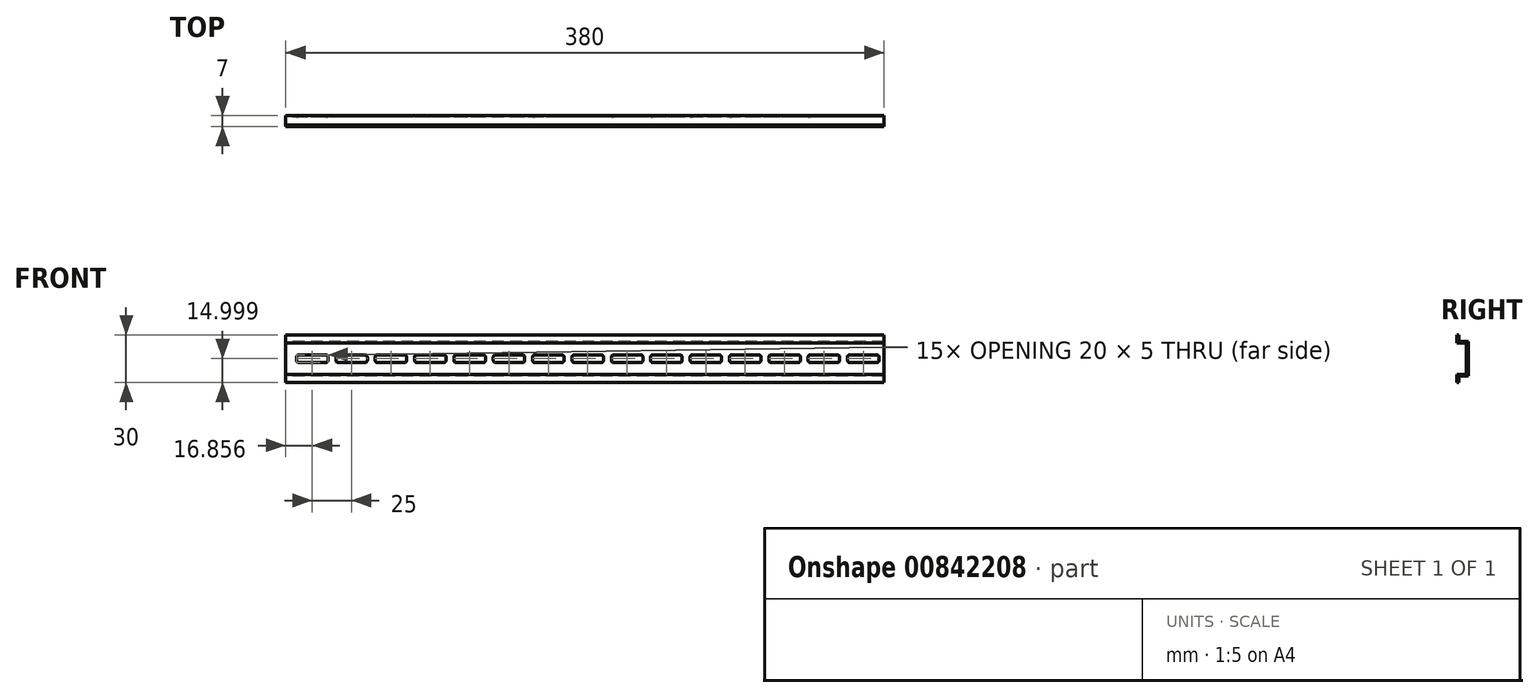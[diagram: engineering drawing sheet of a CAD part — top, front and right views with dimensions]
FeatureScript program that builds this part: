
annotation { "Feature Type Name" : "Feature", "Feature Type Description" : "" }
export const myFeature = defineFeature(function(context is Context, id is Id, definition is map)
    precondition{}
    {
        {
            var Q0;
            Q0=qCreatedBy(makeId("Right.planeOp"),FACE);
            var sketch = newSketch(context, id + "F0", { "sketchPlane" : qUnion([Q0])});
            skLineSegment(sketch, "E0", {"start": v(0, -3.03) * mm, "end": v(0, -25.03) * mm});
            skLineSegment(sketch, "E1", {"start": v(0, -25.03) * mm, "end": v(-6, -25.03) * mm});
            skLineSegment(sketch, "E2", {"start": v(-6, -25.03) * mm, "end": v(-6, -29.03) * mm});
            skLineSegment(sketch, "E3", {"start": v(0, -3.03) * mm, "end": v(-6, -3.03) * mm});
            skLineSegment(sketch, "E4", {"start": v(-6, -3.03) * mm, "end": v(-6, 0.97) * mm});
            skLineSegment(sketch, "E5.1", {"start": v(-7, -24.03) * mm, "end": v(-7, -29.03) * mm});
            skLineSegment(sketch, "E5.2", {"start": v(-1, -24.03) * mm, "end": v(-7, -24.03) * mm});
            skLineSegment(sketch, "E5.3", {"start": v(-1, -4.03) * mm, "end": v(-1, -24.03) * mm});
            skLineSegment(sketch, "E5.4", {"start": v(-1, -4.03) * mm, "end": v(-7, -4.03) * mm});
            skLineSegment(sketch, "E6", {"start": v(-6, -29.03) * mm, "end": v(-7, -29.03) * mm});
            skLineSegment(sketch, "E7", {"start": v(-6, 0.97) * mm, "end": v(-7, 0.97) * mm});
            skLineSegment(sketch, "E8", {"start": v(-7, -4.03) * mm, "end": v(-7, 0.97) * mm});
            skSolve(sketch);
        }
        {
            var Q0;
            Q0=makeQuery(id+"F0.imprint","IMPRINT",FACE,{"disambiguationData":[TD([[makeQuery(id+"F0.imprint","IMPRINT",EDGE,{"derivedFrom":sQuery(id+"F0.wireOp",EDGE,"E0")}),-1.0]])]});
            extrude(context, id + "F1", {"entities" : qUnion([Q0]), "depth" : 380 * mm, "offsetDistance" : 25 * mm});
        }
        {
            var Q0;
            Q0=makeQuery(id+"F1.opExtrude","SWEPT_FACE",FACE,{"disambiguationData":[OSD([sQuery(id+"F0.wireOp",EDGE,"E5.3")])]});
            var sketch = newSketch(context, id + "F2", { "sketchPlane" : qUnion([Q0])});
            skLineSegment(sketch, "E9", {"start": v(0, -14.03) * mm, "end": v(380, -14.03) * mm});
            skLineSegment(sketch, "E10.bottom", {"start": v(25.36, -16.53) * mm, "end": v(8.36, -16.53) * mm});
            skLineSegment(sketch, "E10.top", {"start": v(25.36, -11.53) * mm, "end": v(8.36, -11.53) * mm});
            skLineSegment(sketch, "E10.left", {"start": v(26.86, -15.03) * mm, "end": v(26.86, -13.03) * mm});
            skLineSegment(sketch, "E10.right", {"start": v(6.86, -15.03) * mm, "end": v(6.86, -13.03) * mm});
            skPoint(sketch, "E10.middle", {"position": v(16.86, -14.03) * mm});
            skPoint(sketch, "E11.visualSharp", {"position": v(26.86, -11.53) * mm});
            skArc(sketch, "E11.filletArc", {"start": v(26.86, -13.03) * mm, "mid": v(26.42, -11.97) * mm, "end": v(25.36, -11.53) * mm});
            skPoint(sketch, "E12.visualSharp", {"position": v(26.86, -16.53) * mm});
            skArc(sketch, "E12.filletArc", {"start": v(25.36, -16.53) * mm, "mid": v(26.42, -16.1) * mm, "end": v(26.86, -15.03) * mm});
            skPoint(sketch, "E13.visualSharp", {"position": v(6.86, -11.53) * mm});
            skArc(sketch, "E13.filletArc", {"start": v(8.36, -11.53) * mm, "mid": v(7.3, -11.97) * mm, "end": v(6.86, -13.03) * mm});
            skPoint(sketch, "E14.visualSharp", {"position": v(6.86, -16.53) * mm});
            skArc(sketch, "E14.filletArc", {"start": v(6.86, -15.03) * mm, "mid": v(7.3, -16.1) * mm, "end": v(8.36, -16.53) * mm});
            skLineSegment(sketch, "E15.1.0.0", {"start": v(50.36, -11.53) * mm, "end": v(33.36, -11.53) * mm});
            skLineSegment(sketch, "E15.1.0.1", {"start": v(50.36, -16.53) * mm, "end": v(33.36, -16.53) * mm});
            skArc(sketch, "E15.1.0.2", {"start": v(51.86, -13.03) * mm, "mid": v(51.42, -11.97) * mm, "end": v(50.36, -11.53) * mm});
            skArc(sketch, "E15.1.0.3", {"start": v(50.36, -16.53) * mm, "mid": v(51.42, -16.1) * mm, "end": v(51.86, -15.03) * mm});
            skArc(sketch, "E15.1.0.4", {"start": v(33.36, -11.53) * mm, "mid": v(32.3, -11.97) * mm, "end": v(31.86, -13.03) * mm});
            skArc(sketch, "E15.1.0.5", {"start": v(31.86, -15.03) * mm, "mid": v(32.3, -16.1) * mm, "end": v(33.36, -16.53) * mm});
            skLineSegment(sketch, "E15.2.0.0", {"start": v(75.36, -11.53) * mm, "end": v(58.36, -11.53) * mm});
            skLineSegment(sketch, "E15.2.0.1", {"start": v(75.36, -16.53) * mm, "end": v(58.36, -16.53) * mm});
            skArc(sketch, "E15.2.0.2", {"start": v(76.86, -13.03) * mm, "mid": v(76.42, -11.97) * mm, "end": v(75.36, -11.53) * mm});
            skArc(sketch, "E15.2.0.3", {"start": v(75.36, -16.53) * mm, "mid": v(76.42, -16.1) * mm, "end": v(76.86, -15.03) * mm});
            skArc(sketch, "E15.2.0.4", {"start": v(58.36, -11.53) * mm, "mid": v(57.3, -11.97) * mm, "end": v(56.86, -13.03) * mm});
            skArc(sketch, "E15.2.0.5", {"start": v(56.86, -15.03) * mm, "mid": v(57.3, -16.1) * mm, "end": v(58.36, -16.53) * mm});
            skLineSegment(sketch, "E15.3.0.0", {"start": v(100.36, -11.53) * mm, "end": v(83.36, -11.53) * mm});
            skLineSegment(sketch, "E15.3.0.1", {"start": v(100.36, -16.53) * mm, "end": v(83.36, -16.53) * mm});
            skArc(sketch, "E15.3.0.2", {"start": v(101.86, -13.03) * mm, "mid": v(101.42, -11.97) * mm, "end": v(100.36, -11.53) * mm});
            skArc(sketch, "E15.3.0.3", {"start": v(100.36, -16.53) * mm, "mid": v(101.42, -16.1) * mm, "end": v(101.86, -15.03) * mm});
            skArc(sketch, "E15.3.0.4", {"start": v(83.36, -11.53) * mm, "mid": v(82.3, -11.97) * mm, "end": v(81.86, -13.03) * mm});
            skArc(sketch, "E15.3.0.5", {"start": v(81.86, -15.03) * mm, "mid": v(82.3, -16.1) * mm, "end": v(83.36, -16.53) * mm});
            skLineSegment(sketch, "E15.4.0.0", {"start": v(125.36, -11.53) * mm, "end": v(108.36, -11.53) * mm});
            skLineSegment(sketch, "E15.4.0.1", {"start": v(125.36, -16.53) * mm, "end": v(108.36, -16.53) * mm});
            skArc(sketch, "E15.4.0.2", {"start": v(126.86, -13.03) * mm, "mid": v(126.42, -11.97) * mm, "end": v(125.36, -11.53) * mm});
            skArc(sketch, "E15.4.0.3", {"start": v(125.36, -16.53) * mm, "mid": v(126.42, -16.1) * mm, "end": v(126.86, -15.03) * mm});
            skArc(sketch, "E15.4.0.4", {"start": v(108.36, -11.53) * mm, "mid": v(107.3, -11.97) * mm, "end": v(106.86, -13.03) * mm});
            skArc(sketch, "E15.4.0.5", {"start": v(106.86, -15.03) * mm, "mid": v(107.3, -16.1) * mm, "end": v(108.36, -16.53) * mm});
            skLineSegment(sketch, "E15.5.0.0", {"start": v(150.36, -11.53) * mm, "end": v(133.36, -11.53) * mm});
            skLineSegment(sketch, "E15.5.0.1", {"start": v(150.36, -16.53) * mm, "end": v(133.36, -16.53) * mm});
            skArc(sketch, "E15.5.0.2", {"start": v(151.86, -13.03) * mm, "mid": v(151.42, -11.97) * mm, "end": v(150.36, -11.53) * mm});
            skArc(sketch, "E15.5.0.3", {"start": v(150.36, -16.53) * mm, "mid": v(151.42, -16.1) * mm, "end": v(151.86, -15.03) * mm});
            skArc(sketch, "E15.5.0.4", {"start": v(133.36, -11.53) * mm, "mid": v(132.3, -11.97) * mm, "end": v(131.86, -13.03) * mm});
            skArc(sketch, "E15.5.0.5", {"start": v(131.86, -15.03) * mm, "mid": v(132.3, -16.1) * mm, "end": v(133.36, -16.53) * mm});
            skLineSegment(sketch, "E15.6.0.0", {"start": v(175.36, -11.53) * mm, "end": v(158.36, -11.53) * mm});
            skLineSegment(sketch, "E15.6.0.1", {"start": v(175.36, -16.53) * mm, "end": v(158.36, -16.53) * mm});
            skArc(sketch, "E15.6.0.2", {"start": v(176.86, -13.03) * mm, "mid": v(176.42, -11.97) * mm, "end": v(175.36, -11.53) * mm});
            skArc(sketch, "E15.6.0.3", {"start": v(175.36, -16.53) * mm, "mid": v(176.42, -16.1) * mm, "end": v(176.86, -15.03) * mm});
            skArc(sketch, "E15.6.0.4", {"start": v(158.36, -11.53) * mm, "mid": v(157.3, -11.97) * mm, "end": v(156.86, -13.03) * mm});
            skArc(sketch, "E15.6.0.5", {"start": v(156.86, -15.03) * mm, "mid": v(157.3, -16.1) * mm, "end": v(158.36, -16.53) * mm});
            skLineSegment(sketch, "E15.7.0.0", {"start": v(200.36, -11.53) * mm, "end": v(183.36, -11.53) * mm});
            skLineSegment(sketch, "E15.7.0.1", {"start": v(200.36, -16.53) * mm, "end": v(183.36, -16.53) * mm});
            skArc(sketch, "E15.7.0.2", {"start": v(201.86, -13.03) * mm, "mid": v(201.42, -11.97) * mm, "end": v(200.36, -11.53) * mm});
            skArc(sketch, "E15.7.0.3", {"start": v(200.36, -16.53) * mm, "mid": v(201.42, -16.1) * mm, "end": v(201.86, -15.03) * mm});
            skArc(sketch, "E15.7.0.4", {"start": v(183.36, -11.53) * mm, "mid": v(182.3, -11.97) * mm, "end": v(181.86, -13.03) * mm});
            skArc(sketch, "E15.7.0.5", {"start": v(181.86, -15.03) * mm, "mid": v(182.3, -16.1) * mm, "end": v(183.36, -16.53) * mm});
            skLineSegment(sketch, "E15.8.0.0", {"start": v(225.36, -11.53) * mm, "end": v(208.36, -11.53) * mm});
            skLineSegment(sketch, "E15.8.0.1", {"start": v(225.36, -16.53) * mm, "end": v(208.36, -16.53) * mm});
            skArc(sketch, "E15.8.0.2", {"start": v(226.86, -13.03) * mm, "mid": v(226.42, -11.97) * mm, "end": v(225.36, -11.53) * mm});
            skArc(sketch, "E15.8.0.3", {"start": v(225.36, -16.53) * mm, "mid": v(226.42, -16.1) * mm, "end": v(226.86, -15.03) * mm});
            skArc(sketch, "E15.8.0.4", {"start": v(208.36, -11.53) * mm, "mid": v(207.3, -11.97) * mm, "end": v(206.86, -13.03) * mm});
            skArc(sketch, "E15.8.0.5", {"start": v(206.86, -15.03) * mm, "mid": v(207.3, -16.1) * mm, "end": v(208.36, -16.53) * mm});
            skLineSegment(sketch, "E15.9.0.0", {"start": v(250.36, -11.53) * mm, "end": v(233.36, -11.53) * mm});
            skLineSegment(sketch, "E15.9.0.1", {"start": v(250.36, -16.53) * mm, "end": v(233.36, -16.53) * mm});
            skArc(sketch, "E15.9.0.2", {"start": v(251.86, -13.03) * mm, "mid": v(251.42, -11.97) * mm, "end": v(250.36, -11.53) * mm});
            skArc(sketch, "E15.9.0.3", {"start": v(250.36, -16.53) * mm, "mid": v(251.42, -16.1) * mm, "end": v(251.86, -15.03) * mm});
            skArc(sketch, "E15.9.0.4", {"start": v(233.36, -11.53) * mm, "mid": v(232.3, -11.97) * mm, "end": v(231.86, -13.03) * mm});
            skArc(sketch, "E15.9.0.5", {"start": v(231.86, -15.03) * mm, "mid": v(232.3, -16.1) * mm, "end": v(233.36, -16.53) * mm});
            skLineSegment(sketch, "E15.10.0.0", {"start": v(275.36, -11.53) * mm, "end": v(258.36, -11.53) * mm});
            skLineSegment(sketch, "E15.10.0.1", {"start": v(275.36, -16.53) * mm, "end": v(258.36, -16.53) * mm});
            skArc(sketch, "E15.10.0.2", {"start": v(276.86, -13.03) * mm, "mid": v(276.42, -11.97) * mm, "end": v(275.36, -11.53) * mm});
            skArc(sketch, "E15.10.0.3", {"start": v(275.36, -16.53) * mm, "mid": v(276.42, -16.1) * mm, "end": v(276.86, -15.03) * mm});
            skArc(sketch, "E15.10.0.4", {"start": v(258.36, -11.53) * mm, "mid": v(257.3, -11.97) * mm, "end": v(256.86, -13.03) * mm});
            skArc(sketch, "E15.10.0.5", {"start": v(256.86, -15.03) * mm, "mid": v(257.3, -16.1) * mm, "end": v(258.36, -16.53) * mm});
            skLineSegment(sketch, "E15.11.0.0", {"start": v(300.36, -11.53) * mm, "end": v(283.36, -11.53) * mm});
            skLineSegment(sketch, "E15.11.0.1", {"start": v(300.36, -16.53) * mm, "end": v(283.36, -16.53) * mm});
            skArc(sketch, "E15.11.0.2", {"start": v(301.86, -13.03) * mm, "mid": v(301.42, -11.97) * mm, "end": v(300.36, -11.53) * mm});
            skArc(sketch, "E15.11.0.3", {"start": v(300.36, -16.53) * mm, "mid": v(301.42, -16.1) * mm, "end": v(301.86, -15.03) * mm});
            skArc(sketch, "E15.11.0.4", {"start": v(283.36, -11.53) * mm, "mid": v(282.3, -11.97) * mm, "end": v(281.86, -13.03) * mm});
            skArc(sketch, "E15.11.0.5", {"start": v(281.86, -15.03) * mm, "mid": v(282.3, -16.1) * mm, "end": v(283.36, -16.53) * mm});
            skLineSegment(sketch, "E15.12.0.0", {"start": v(325.36, -11.53) * mm, "end": v(308.36, -11.53) * mm});
            skLineSegment(sketch, "E15.12.0.1", {"start": v(325.36, -16.53) * mm, "end": v(308.36, -16.53) * mm});
            skArc(sketch, "E15.12.0.2", {"start": v(326.86, -13.03) * mm, "mid": v(326.42, -11.97) * mm, "end": v(325.36, -11.53) * mm});
            skArc(sketch, "E15.12.0.3", {"start": v(325.36, -16.53) * mm, "mid": v(326.42, -16.1) * mm, "end": v(326.86, -15.03) * mm});
            skArc(sketch, "E15.12.0.4", {"start": v(308.36, -11.53) * mm, "mid": v(307.3, -11.97) * mm, "end": v(306.86, -13.03) * mm});
            skArc(sketch, "E15.12.0.5", {"start": v(306.86, -15.03) * mm, "mid": v(307.3, -16.1) * mm, "end": v(308.36, -16.53) * mm});
            skLineSegment(sketch, "E15.13.0.0", {"start": v(350.36, -11.53) * mm, "end": v(333.36, -11.53) * mm});
            skLineSegment(sketch, "E15.13.0.1", {"start": v(350.36, -16.53) * mm, "end": v(333.36, -16.53) * mm});
            skArc(sketch, "E15.13.0.2", {"start": v(351.86, -13.03) * mm, "mid": v(351.42, -11.97) * mm, "end": v(350.36, -11.53) * mm});
            skArc(sketch, "E15.13.0.3", {"start": v(350.36, -16.53) * mm, "mid": v(351.42, -16.1) * mm, "end": v(351.86, -15.03) * mm});
            skArc(sketch, "E15.13.0.4", {"start": v(333.36, -11.53) * mm, "mid": v(332.3, -11.97) * mm, "end": v(331.86, -13.03) * mm});
            skArc(sketch, "E15.13.0.5", {"start": v(331.86, -15.03) * mm, "mid": v(332.3, -16.1) * mm, "end": v(333.36, -16.53) * mm});
            skLineSegment(sketch, "E15.14.0.0", {"start": v(375.36, -11.53) * mm, "end": v(358.36, -11.53) * mm});
            skLineSegment(sketch, "E15.14.0.1", {"start": v(375.36, -16.53) * mm, "end": v(358.36, -16.53) * mm});
            skArc(sketch, "E15.14.0.2", {"start": v(376.86, -13.03) * mm, "mid": v(376.42, -11.97) * mm, "end": v(375.36, -11.53) * mm});
            skArc(sketch, "E15.14.0.3", {"start": v(375.36, -16.53) * mm, "mid": v(376.42, -16.1) * mm, "end": v(376.86, -15.03) * mm});
            skArc(sketch, "E15.14.0.4", {"start": v(358.36, -11.53) * mm, "mid": v(357.3, -11.97) * mm, "end": v(356.86, -13.03) * mm});
            skArc(sketch, "E15.14.0.5", {"start": v(356.86, -15.03) * mm, "mid": v(357.3, -16.1) * mm, "end": v(358.36, -16.53) * mm});
            skLineSegment(sketch, "E15.direction1", {"start": v(8.36, -11.53) * mm, "end": v(33.36, -11.53) * mm, "construction": true});
            skLineSegment(sketch, "E16.1.0.0", {"start": v(31.86, -15.03) * mm, "end": v(31.86, -13.03) * mm});
            skLineSegment(sketch, "E16.1.0.1", {"start": v(51.86, -15.03) * mm, "end": v(51.86, -13.03) * mm});
            skLineSegment(sketch, "E16.2.0.0", {"start": v(56.86, -15.03) * mm, "end": v(56.86, -13.03) * mm});
            skLineSegment(sketch, "E16.2.0.1", {"start": v(76.86, -15.03) * mm, "end": v(76.86, -13.03) * mm});
            skLineSegment(sketch, "E16.3.0.0", {"start": v(81.86, -15.03) * mm, "end": v(81.86, -13.03) * mm});
            skLineSegment(sketch, "E16.3.0.1", {"start": v(101.86, -15.03) * mm, "end": v(101.86, -13.03) * mm});
            skLineSegment(sketch, "E16.4.0.0", {"start": v(106.86, -15.03) * mm, "end": v(106.86, -13.03) * mm});
            skLineSegment(sketch, "E16.4.0.1", {"start": v(126.86, -15.03) * mm, "end": v(126.86, -13.03) * mm});
            skLineSegment(sketch, "E16.5.0.0", {"start": v(131.86, -15.03) * mm, "end": v(131.86, -13.03) * mm});
            skLineSegment(sketch, "E16.5.0.1", {"start": v(151.86, -15.03) * mm, "end": v(151.86, -13.03) * mm});
            skLineSegment(sketch, "E16.6.0.0", {"start": v(156.86, -15.03) * mm, "end": v(156.86, -13.03) * mm});
            skLineSegment(sketch, "E16.6.0.1", {"start": v(176.86, -15.03) * mm, "end": v(176.86, -13.03) * mm});
            skLineSegment(sketch, "E16.7.0.0", {"start": v(181.86, -15.03) * mm, "end": v(181.86, -13.03) * mm});
            skLineSegment(sketch, "E16.7.0.1", {"start": v(201.86, -15.03) * mm, "end": v(201.86, -13.03) * mm});
            skLineSegment(sketch, "E16.8.0.0", {"start": v(206.86, -15.03) * mm, "end": v(206.86, -13.03) * mm});
            skLineSegment(sketch, "E16.8.0.1", {"start": v(226.86, -15.03) * mm, "end": v(226.86, -13.03) * mm});
            skLineSegment(sketch, "E16.9.0.0", {"start": v(231.86, -15.03) * mm, "end": v(231.86, -13.03) * mm});
            skLineSegment(sketch, "E16.9.0.1", {"start": v(251.86, -15.03) * mm, "end": v(251.86, -13.03) * mm});
            skLineSegment(sketch, "E16.10.0.0", {"start": v(256.86, -15.03) * mm, "end": v(256.86, -13.03) * mm});
            skLineSegment(sketch, "E16.10.0.1", {"start": v(276.86, -15.03) * mm, "end": v(276.86, -13.03) * mm});
            skLineSegment(sketch, "E16.11.0.0", {"start": v(281.86, -15.03) * mm, "end": v(281.86, -13.03) * mm});
            skLineSegment(sketch, "E16.11.0.1", {"start": v(301.86, -15.03) * mm, "end": v(301.86, -13.03) * mm});
            skLineSegment(sketch, "E16.12.0.0", {"start": v(306.86, -15.03) * mm, "end": v(306.86, -13.03) * mm});
            skLineSegment(sketch, "E16.12.0.1", {"start": v(326.86, -15.03) * mm, "end": v(326.86, -13.03) * mm});
            skLineSegment(sketch, "E16.13.0.0", {"start": v(331.86, -15.03) * mm, "end": v(331.86, -13.03) * mm});
            skLineSegment(sketch, "E16.13.0.1", {"start": v(351.86, -15.03) * mm, "end": v(351.86, -13.03) * mm});
            skLineSegment(sketch, "E16.14.0.0", {"start": v(356.86, -15.03) * mm, "end": v(356.86, -13.03) * mm});
            skLineSegment(sketch, "E16.14.0.1", {"start": v(376.86, -15.03) * mm, "end": v(376.86, -13.03) * mm});
            skLineSegment(sketch, "E16.direction1", {"start": v(6.86, -15.03) * mm, "end": v(31.86, -15.03) * mm, "construction": true});
            skSolve(sketch);
        }
        {
            var Q0;
            Q0=makeQuery(id+"F2.imprint","IMPRINT",FACE,{"disambiguationData":[TD([[makeQuery(id+"F2.imprint","IMPRINT",EDGE,{"derivedFrom":sQuery(id+"F2.wireOp",EDGE,"E10.top")}),1.0]])]});
            var Q1;
            Q1=makeQuery(id+"F2.imprint","IMPRINT",FACE,{"disambiguationData":[TD([[makeQuery(id+"F2.imprint","IMPRINT",EDGE,{"derivedFrom":sQuery(id+"F2.wireOp",EDGE,"E10.bottom")}),-1.0]])]});
            var Q2;
            Q2=makeQuery(id+"F2.imprint","IMPRINT",FACE,{"disambiguationData":[TD([[makeQuery(id+"F2.imprint","IMPRINT",EDGE,{"derivedFrom":sQuery(id+"F2.wireOp",EDGE,"E15.1.0.0")}),1.0]])]});
            var Q3;
            Q3=makeQuery(id+"F2.imprint","IMPRINT",FACE,{"disambiguationData":[TD([[makeQuery(id+"F2.imprint","IMPRINT",EDGE,{"derivedFrom":sQuery(id+"F2.wireOp",EDGE,"E15.1.0.1")}),-1.0]])]});
            var Q4;
            Q4=makeQuery(id+"F2.imprint","IMPRINT",FACE,{"disambiguationData":[TD([[makeQuery(id+"F2.imprint","IMPRINT",EDGE,{"derivedFrom":sQuery(id+"F2.wireOp",EDGE,"E15.2.0.0")}),1.0]])]});
            var Q5;
            Q5=makeQuery(id+"F2.imprint","IMPRINT",FACE,{"disambiguationData":[TD([[makeQuery(id+"F2.imprint","IMPRINT",EDGE,{"derivedFrom":sQuery(id+"F2.wireOp",EDGE,"E15.2.0.1")}),-1.0]])]});
            var Q6;
            Q6=makeQuery(id+"F2.imprint","IMPRINT",FACE,{"disambiguationData":[TD([[makeQuery(id+"F2.imprint","IMPRINT",EDGE,{"derivedFrom":sQuery(id+"F2.wireOp",EDGE,"E15.3.0.0")}),1.0]])]});
            var Q7;
            Q7=makeQuery(id+"F2.imprint","IMPRINT",FACE,{"disambiguationData":[TD([[makeQuery(id+"F2.imprint","IMPRINT",EDGE,{"derivedFrom":sQuery(id+"F2.wireOp",EDGE,"E15.3.0.1")}),-1.0]])]});
            var Q8;
            Q8=makeQuery(id+"F2.imprint","IMPRINT",FACE,{"disambiguationData":[TD([[makeQuery(id+"F2.imprint","IMPRINT",EDGE,{"derivedFrom":sQuery(id+"F2.wireOp",EDGE,"E15.4.0.0")}),1.0]])]});
            var Q9;
            Q9=makeQuery(id+"F2.imprint","IMPRINT",FACE,{"disambiguationData":[TD([[makeQuery(id+"F2.imprint","IMPRINT",EDGE,{"derivedFrom":sQuery(id+"F2.wireOp",EDGE,"E15.4.0.1")}),-1.0]])]});
            var Q10;
            Q10=makeQuery(id+"F2.imprint","IMPRINT",FACE,{"disambiguationData":[TD([[makeQuery(id+"F2.imprint","IMPRINT",EDGE,{"derivedFrom":sQuery(id+"F2.wireOp",EDGE,"E15.5.0.0")}),1.0]])]});
            var Q11;
            Q11=makeQuery(id+"F2.imprint","IMPRINT",FACE,{"disambiguationData":[TD([[makeQuery(id+"F2.imprint","IMPRINT",EDGE,{"derivedFrom":sQuery(id+"F2.wireOp",EDGE,"E15.5.0.1")}),-1.0]])]});
            var Q12;
            Q12=makeQuery(id+"F2.imprint","IMPRINT",FACE,{"disambiguationData":[TD([[makeQuery(id+"F2.imprint","IMPRINT",EDGE,{"derivedFrom":sQuery(id+"F2.wireOp",EDGE,"E15.6.0.1")}),-1.0]])]});
            var Q13;
            Q13=makeQuery(id+"F2.imprint","IMPRINT",FACE,{"disambiguationData":[TD([[makeQuery(id+"F2.imprint","IMPRINT",EDGE,{"derivedFrom":sQuery(id+"F2.wireOp",EDGE,"E15.6.0.0")}),1.0]])]});
            var Q14;
            Q14=makeQuery(id+"F2.imprint","IMPRINT",FACE,{"disambiguationData":[TD([[makeQuery(id+"F2.imprint","IMPRINT",EDGE,{"derivedFrom":sQuery(id+"F2.wireOp",EDGE,"E15.7.0.0")}),1.0]])]});
            var Q15;
            Q15=makeQuery(id+"F2.imprint","IMPRINT",FACE,{"disambiguationData":[TD([[makeQuery(id+"F2.imprint","IMPRINT",EDGE,{"derivedFrom":sQuery(id+"F2.wireOp",EDGE,"E15.7.0.1")}),-1.0]])]});
            var Q16;
            Q16=makeQuery(id+"F2.imprint","IMPRINT",FACE,{"disambiguationData":[TD([[makeQuery(id+"F2.imprint","IMPRINT",EDGE,{"derivedFrom":sQuery(id+"F2.wireOp",EDGE,"E15.8.0.1")}),-1.0]])]});
            var Q17;
            Q17=makeQuery(id+"F2.imprint","IMPRINT",FACE,{"disambiguationData":[TD([[makeQuery(id+"F2.imprint","IMPRINT",EDGE,{"derivedFrom":sQuery(id+"F2.wireOp",EDGE,"E15.8.0.0")}),1.0]])]});
            var Q18;
            Q18=makeQuery(id+"F2.imprint","IMPRINT",FACE,{"disambiguationData":[TD([[makeQuery(id+"F2.imprint","IMPRINT",EDGE,{"derivedFrom":sQuery(id+"F2.wireOp",EDGE,"E15.9.0.1")}),-1.0]])]});
            var Q19;
            Q19=makeQuery(id+"F2.imprint","IMPRINT",FACE,{"disambiguationData":[TD([[makeQuery(id+"F2.imprint","IMPRINT",EDGE,{"derivedFrom":sQuery(id+"F2.wireOp",EDGE,"E15.9.0.0")}),1.0]])]});
            var Q20;
            Q20=makeQuery(id+"F2.imprint","IMPRINT",FACE,{"disambiguationData":[TD([[makeQuery(id+"F2.imprint","IMPRINT",EDGE,{"derivedFrom":sQuery(id+"F2.wireOp",EDGE,"E15.10.0.1")}),-1.0]])]});
            var Q21;
            Q21=makeQuery(id+"F2.imprint","IMPRINT",FACE,{"disambiguationData":[TD([[makeQuery(id+"F2.imprint","IMPRINT",EDGE,{"derivedFrom":sQuery(id+"F2.wireOp",EDGE,"E15.10.0.0")}),1.0]])]});
            var Q22;
            Q22=makeQuery(id+"F2.imprint","IMPRINT",FACE,{"disambiguationData":[TD([[makeQuery(id+"F2.imprint","IMPRINT",EDGE,{"derivedFrom":sQuery(id+"F2.wireOp",EDGE,"E15.11.0.1")}),-1.0]])]});
            var Q23;
            Q23=makeQuery(id+"F2.imprint","IMPRINT",FACE,{"disambiguationData":[TD([[makeQuery(id+"F2.imprint","IMPRINT",EDGE,{"derivedFrom":sQuery(id+"F2.wireOp",EDGE,"E15.11.0.0")}),1.0]])]});
            var Q24;
            Q24=makeQuery(id+"F2.imprint","IMPRINT",FACE,{"disambiguationData":[TD([[makeQuery(id+"F2.imprint","IMPRINT",EDGE,{"derivedFrom":sQuery(id+"F2.wireOp",EDGE,"E15.12.0.0")}),1.0]])]});
            var Q25;
            Q25=makeQuery(id+"F2.imprint","IMPRINT",FACE,{"disambiguationData":[TD([[makeQuery(id+"F2.imprint","IMPRINT",EDGE,{"derivedFrom":sQuery(id+"F2.wireOp",EDGE,"E15.12.0.1")}),-1.0]])]});
            var Q26;
            Q26=makeQuery(id+"F2.imprint","IMPRINT",FACE,{"disambiguationData":[TD([[makeQuery(id+"F2.imprint","IMPRINT",EDGE,{"derivedFrom":sQuery(id+"F2.wireOp",EDGE,"E15.13.0.1")}),-1.0]])]});
            var Q27;
            Q27=makeQuery(id+"F2.imprint","IMPRINT",FACE,{"disambiguationData":[TD([[makeQuery(id+"F2.imprint","IMPRINT",EDGE,{"derivedFrom":sQuery(id+"F2.wireOp",EDGE,"E15.13.0.0")}),1.0]])]});
            var Q28;
            Q28=makeQuery(id+"F2.imprint","IMPRINT",FACE,{"disambiguationData":[TD([[makeQuery(id+"F2.imprint","IMPRINT",EDGE,{"derivedFrom":sQuery(id+"F2.wireOp",EDGE,"E15.14.0.0")}),1.0]])]});
            var Q29;
            Q29=makeQuery(id+"F2.imprint","IMPRINT",FACE,{"disambiguationData":[TD([[makeQuery(id+"F2.imprint","IMPRINT",EDGE,{"derivedFrom":sQuery(id+"F2.wireOp",EDGE,"E15.14.0.1")}),-1.0]])]});
            extrude(context, id + "F3", {"entities" : qUnion([Q0, Q1, Q2, Q3, Q4, Q5, Q6, Q7, Q8, Q9, Q10, Q11, Q12, Q13, Q14, Q15, Q16, Q17, Q18, Q19, Q20, Q21, Q22, Q23, Q24, Q25, Q26, Q27, Q28, Q29]), "operationType" : NewBodyOperationType.REMOVE, "oppositeDirection" : true, "depth" : 25 * mm, "offsetDistance" : 25 * mm});
        }
    });
